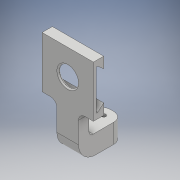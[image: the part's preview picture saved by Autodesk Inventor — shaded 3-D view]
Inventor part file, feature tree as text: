
AUTODESK INVENTOR PART (.ipt)
format: ipt  version: 2017 (Build 210142000, 142)  size: 195,072 bytes
history: native  units: mm
features: extrude x5, fillet x5, sketch x4, hole x1
ambient origin geometry x8: Origin, YZ Plane, XZ Plane, XY Plane, X Axis, Y Axis, Z Axis, Center Point
bodies: Solid1 (feature_tree)
feature tree (15):
  extrude  "Block"  Depth=12.0mm
  extrude  "Tripod Slot"  Depth=60.0mm
  hole  "Hole1"  [1 undecoded]
  extrude  "Extrusion4"  Depth=1.5mm
  extrude  "Extrusion5"  Depth=1.5mm
  extrude  "Extrusion6"  Depth=1.5mm
  fillet  "Fillet4"  Radius=60.0mm
  fillet  "Fillet5"  Radius=30.0mm
  fillet  "Fillet6"  Radius=52.5mm
  fillet  "Fillet10"  Radius=40.0mm
  fillet  "Fillet11"  Radius=5.0mm
  sketch  "Sketch2"  dims[d0=60.0mm d1=12.0mm]
  sketch  "Sketch4"  dims[d14=60.0mm d15=0.0mm d17=17.25mm]
  sketch  "Sketch5"  dims[d18=17.25mm d19=8.9mm]
  sketch  "Sketch6"  dims[d20=23.25mm d21=23.25mm d22=2.0mm d23=2.0mm d24=60.0mm d25=0.0mm d46=30.0mm d47=30.0mm d48=22.5mm d49=6.0mm d50=4.0mm d51=2.0mm d52=90.0deg d53=8.0mm d54=20.594885mm d55=52.5mm d56=0.0mm d58=40.0mm d59=0.0mm d60=5.0mm d61=10.0mm d62=31.75mm d63=0.0mm d64=25.4mm d65=4.413583mm d66=17.3mm d67=22.5mm d68=3.0mm d70=11.0mm d71=20.0mm d72=5.0mm d94=7.5mm d95=1.5mm]
note: 1 required parameter value undecoded (feature->parameter linkage not recoverable at this tier; creation-order binding heuristic only, values carry confidence <= 0.55)
